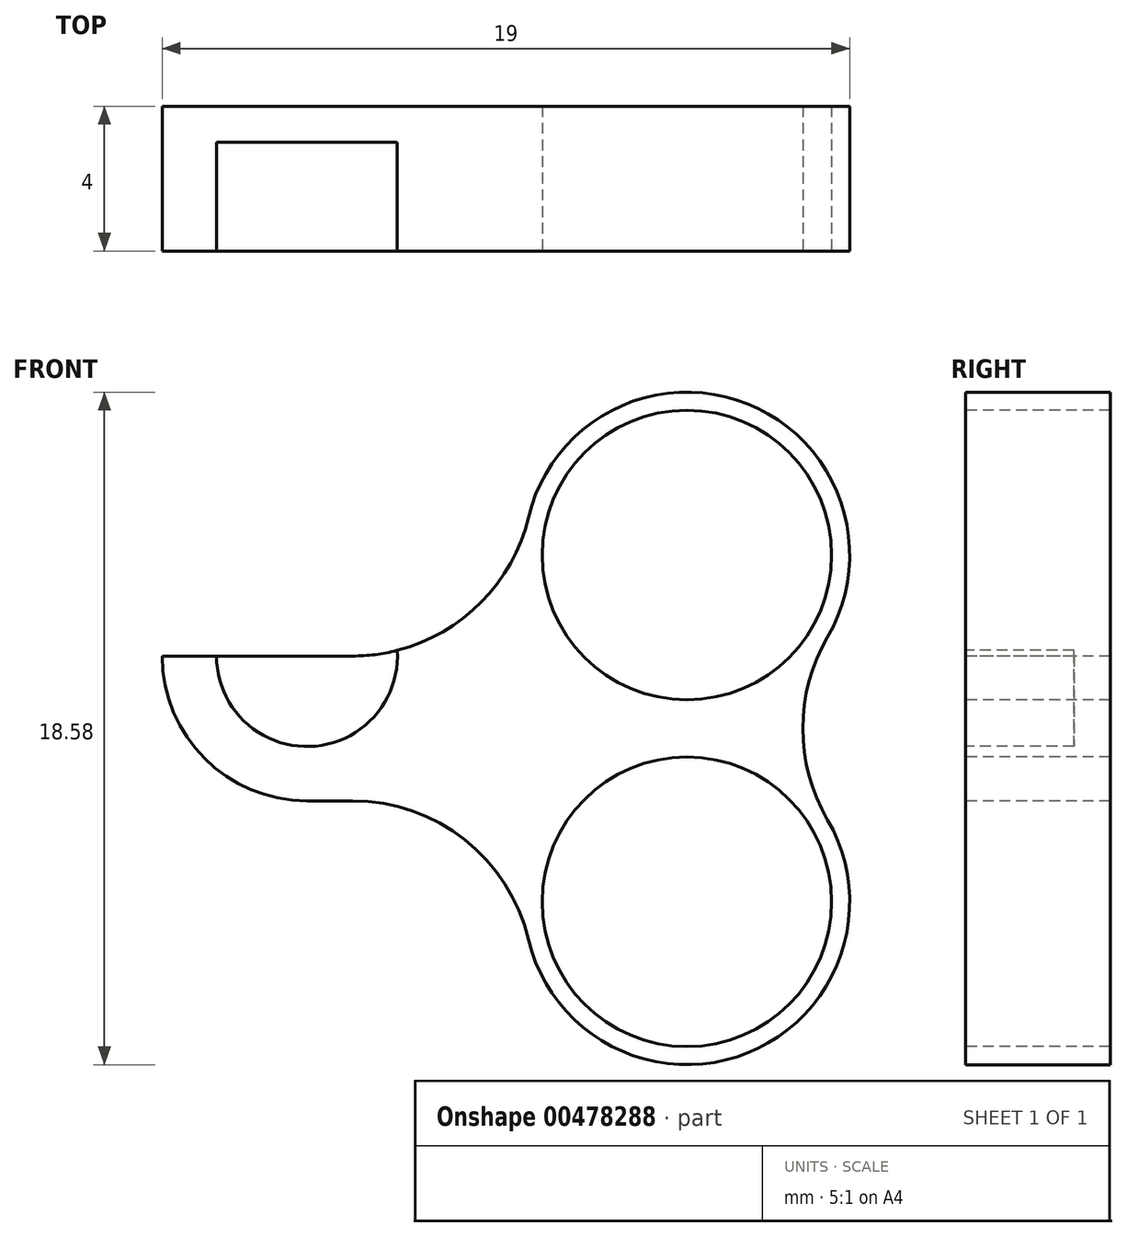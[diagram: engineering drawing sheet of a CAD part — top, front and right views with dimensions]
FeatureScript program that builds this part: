
annotation { "Feature Type Name" : "Feature", "Feature Type Description" : "" }
export const myFeature = defineFeature(function(context is Context, id is Id, definition is map)
    precondition{}
    {
        {
            var Q0;
            Q0=qCreatedBy(makeId("Front.planeOp"),FACE);
            var sketch = newSketch(context, id + "F0", { "sketchPlane" : qUnion([Q0])});
            skLineSegment(sketch, "E0.bottom", {"start": v(-4.5, 4.5) * mm, "end": v(4.5, 4.5) * mm});
            skLineSegment(sketch, "E0.top", {"start": v(-4.5, -14.08) * mm, "end": v(4.5, -14.08) * mm});
            skLineSegment(sketch, "E0.left", {"start": v(-4.5, 4.5) * mm, "end": v(-4.5, -14.08) * mm});
            skLineSegment(sketch, "E0.right", {"start": v(4.5, 4.5) * mm, "end": v(4.5, -14.08) * mm});
            skCircle(sketch, "E1", {"center": v(0, 0) * mm, "radius": 4 * mm});
            skCircle(sketch, "E2", {"center": v(0, -9.58) * mm, "radius": 4 * mm});
            skPoint(sketch, "E3", {"position": v(0, 4.5) * mm});
            skLineSegment(sketch, "E4.bottom", {"start": v(-14.5, -2.79) * mm, "end": v(0, -2.8) * mm});
            skLineSegment(sketch, "E4.left", {"start": v(-14.5, -2.79) * mm, "end": v(-14.5, -6.8) * mm});
            skLineSegment(sketch, "E4.right", {"start": v(0, -2.8) * mm, "end": v(0, -6.8) * mm});
            skLineSegment(sketch, "E5", {"start": v(-14.5, -6.79) * mm, "end": v(0, -6.8) * mm});
            skPoint(sketch, "E6", {"position": v(-10.5, -2.79) * mm});
            skCircle(sketch, "E7", {"center": v(-10.5, -2.79) * mm, "radius": 2.5 * mm});
            skCircle(sketch, "E8.0", {"center": v(0, 0) * mm, "radius": 4.5 * mm});
            skCircle(sketch, "E9.0", {"center": v(0, -9.58) * mm, "radius": 4.5 * mm});
            skPoint(sketch, "E10", {"position": v(4.5, -4.8) * mm});
            skPoint(sketch, "E11", {"position": v(0, -4.8) * mm});
            skCircle(sketch, "E12", {"center": v(8.2, -4.79) * mm, "radius": 5 * mm});
            skSolve(sketch);
        }
        {
            var Q0;
            {var subQ4=sQuery(id+"F0.wireOp",EDGE,"E1");var subQ7=sQuery(id+"F0.wireOp",EDGE,"E4.bottom");var subQ8=makeQuery(id+"F0.imprint","INTERSECT",VERTEX,{"derivedFrom":[subQ4,subQ7]});Q0=makeQuery(id+"F0.imprint","IMPRINT",FACE,{"disambiguationData":[TD([[makeQuery(id+"F0.imprint","IMPRINT",EDGE,{"disambiguationData":[TD([[subQ8,1.0]])],"derivedFrom":subQ4}),-1.0]])]});}
            var Q1;
            {var subQ2=sQuery(id+"F0.wireOp",EDGE,"E4.right");var subQ4=sQuery(id+"F0.wireOp",EDGE,"E2");var subQ5=makeQuery(id+"F0.imprint","INTERSECT",VERTEX,{"derivedFrom":[subQ4,subQ2]});Q1=makeQuery(id+"F0.imprint","IMPRINT",FACE,{"disambiguationData":[TD([[makeQuery(id+"F0.imprint","IMPRINT",EDGE,{"disambiguationData":[TD([[subQ5,1.0]])],"derivedFrom":subQ4}),-1.0]])]});}
            var Q2;
            {var subQ0=sQuery(id+"F0.wireOp",EDGE,"E4.bottom");var subQ1=sQuery(id+"F0.wireOp",EDGE,"E1");var subQ2=makeQuery(id+"F0.imprint","INTERSECT",VERTEX,{"derivedFrom":[subQ1,subQ0]});Q2=makeQuery(id+"F0.imprint","IMPRINT",FACE,{"disambiguationData":[TD([[makeQuery(id+"F0.imprint","IMPRINT",EDGE,{"disambiguationData":[TD([[subQ2,-1.0]])],"derivedFrom":subQ1}),-1.0]])]});}
            var Q3;
            {var subQ0=sQuery(id+"F0.wireOp",EDGE,"E4.right");var subQ1=sQuery(id+"F0.wireOp",EDGE,"E2");var subQ2=makeQuery(id+"F0.imprint","INTERSECT",VERTEX,{"derivedFrom":[subQ1,subQ0]});Q3=makeQuery(id+"F0.imprint","IMPRINT",FACE,{"disambiguationData":[TD([[makeQuery(id+"F0.imprint","IMPRINT",EDGE,{"disambiguationData":[TD([[subQ2,-1.0]])],"derivedFrom":subQ1}),-1.0]])]});}
            var Q4;
            {var subQ6=sQuery(id+"F0.wireOp",EDGE,"E0.left");var subQ9=sQuery(id+"F0.wireOp",EDGE,"E4.bottom");var subQ10=makeQuery(id+"F0.imprint","INTERSECT",VERTEX,{"derivedFrom":[subQ6,subQ9]});Q4=makeQuery(id+"F0.imprint","IMPRINT",FACE,{"disambiguationData":[TD([[makeQuery(id+"F0.imprint","IMPRINT",EDGE,{"disambiguationData":[TD([[subQ10,-1.0]])],"derivedFrom":subQ6}),1.0]])]});}
            var Q5;
            {var subQ0=sQuery(id+"F0.wireOp",EDGE,"E8.0");var subQ1=sQuery(id+"F0.wireOp",EDGE,"E0.left");var subQ2=makeQuery(id+"F0.imprint","INTERSECT",VERTEX,{"derivedFrom":[subQ1,subQ0]});Q5=makeQuery(id+"F0.imprint","IMPRINT",FACE,{"disambiguationData":[TD([[makeQuery(id+"F0.imprint","IMPRINT",EDGE,{"disambiguationData":[TD([[subQ2,-1.0]])],"derivedFrom":subQ1}),1.0]])]});}
            var Q6;
            {var subQ0=sQuery(id+"F0.wireOp",EDGE,"E5");var subQ1=sQuery(id+"F0.wireOp",EDGE,"E0.left");var subQ2=makeQuery(id+"F0.imprint","INTERSECT",VERTEX,{"derivedFrom":[subQ1,subQ0]});Q6=makeQuery(id+"F0.imprint","IMPRINT",FACE,{"disambiguationData":[TD([[makeQuery(id+"F0.imprint","IMPRINT",EDGE,{"disambiguationData":[TD([[subQ2,-1.0]])],"derivedFrom":subQ1}),1.0]])]});}
            var Q7;
            {var subQ0=sQuery(id+"F0.wireOp",EDGE,"E4.left");Q7=makeQuery(id+"F0.imprint","IMPRINT",FACE,{"disambiguationData":[TD([[makeQuery(id+"F0.imprint","IMPRINT",EDGE,{"derivedFrom":subQ0}),1.0]])]});}
            var Q8;
            {var subQ0=sQuery(id+"F0.wireOp",EDGE,"E7");var subQ1=sQuery(id+"F0.wireOp",EDGE,"E4.bottom");var subQ2=makeQuery(id+"F0.imprint","INTERSECT",VERTEX,{"disambiguationData":[OD(0.0)],"derivedFrom":[subQ1,subQ0]});Q8=makeQuery(id+"F0.imprint","IMPRINT",FACE,{"disambiguationData":[TD([[makeQuery(id+"F0.imprint","IMPRINT",EDGE,{"disambiguationData":[TD([[subQ2,-1.0]])],"derivedFrom":subQ1}),-1.0]])]});}
            var Q9;
            {var subQ0=sQuery(id+"F0.wireOp",EDGE,"E8.0");var subQ1=sQuery(id+"F0.wireOp",EDGE,"E4.right");var subQ2=makeQuery(id+"F0.imprint","INTERSECT",VERTEX,{"derivedFrom":[subQ1,subQ0]});Q9=makeQuery(id+"F0.imprint","IMPRINT",FACE,{"disambiguationData":[TD([[makeQuery(id+"F0.imprint","IMPRINT",EDGE,{"disambiguationData":[TD([[subQ2,-1.0]])],"derivedFrom":subQ1}),1.0]])]});}
            extrude(context, id + "F1", {"entities" : qUnion([Q0, Q1, Q2, Q3, Q4, Q5, Q6, Q7, Q8, Q9]), "oppositeDirection" : true, "depth" : 4 * mm});
        }
        {
            var Q0;
            Q0=makeQuery(id+"F1.opExtrude","SWEPT_EDGE",EDGE,{"disambiguationData":[OSD([sQuery(id+"F0.wireOp",EDGE,"E0.left"),sQuery(id+"F0.wireOp",EDGE,"E4.bottom")])]});
            var Q1;
            Q1=makeQuery(id+"F1.opExtrude","SWEPT_EDGE",EDGE,{"disambiguationData":[OSD([sQuery(id+"F0.wireOp",EDGE,"E0.left"),sQuery(id+"F0.wireOp",EDGE,"E5")])]});
            fillet(context, id + "F2", {"entities" : qUnion([Q0, Q1]), "radius" : 5 * mm, "tangentPropagation" : true, "allowEdgeOverflow" : false});
        }
        {
            var Q0;
            Q0=makeQuery(id+"F1.opExtrude","SWEPT_EDGE",EDGE,{"disambiguationData":[OSD([sQuery(id+"F0.wireOp",EDGE,"E4.left"),sQuery(id+"F0.wireOp",EDGE,"E5")])]});
            fillet(context, id + "F3", {"entities" : qUnion([Q0]), "radius" : 4 * mm, "tangentPropagation" : true, "allowEdgeOverflow" : false});
        }
        {
            var Q0;
            {var subQ0=sQuery(id+"F0.wireOp",EDGE,"E7");var subQ1=sQuery(id+"F0.wireOp",EDGE,"E4.bottom");var subQ2=makeQuery(id+"F0.imprint","INTERSECT",VERTEX,{"disambiguationData":[OD(0.0)],"derivedFrom":[subQ1,subQ0]});Q0=makeQuery(id+"F0.imprint","IMPRINT",FACE,{"disambiguationData":[TD([[makeQuery(id+"F0.imprint","IMPRINT",EDGE,{"disambiguationData":[TD([[subQ2,-1.0]])],"derivedFrom":subQ1}),-1.0]])]});}
            var Q1;
            {var subQ0=sQuery(id+"F0.wireOp",EDGE,"E7");var subQ1=sQuery(id+"F0.wireOp",EDGE,"E4.bottom");var subQ2=makeQuery(id+"F0.imprint","INTERSECT",VERTEX,{"disambiguationData":[OD(0.0)],"derivedFrom":[subQ1,subQ0]});Q1=makeQuery(id+"F0.imprint","IMPRINT",FACE,{"disambiguationData":[TD([[makeQuery(id+"F0.imprint","IMPRINT",EDGE,{"disambiguationData":[TD([[subQ2,-1.0]])],"derivedFrom":subQ1}),1.0]])]});}
            extrude(context, id + "F4", {"entities" : qUnion([Q0, Q1]), "operationType" : NewBodyOperationType.REMOVE, "oppositeDirection" : true, "depth" : 3 * mm});
        }
    });
